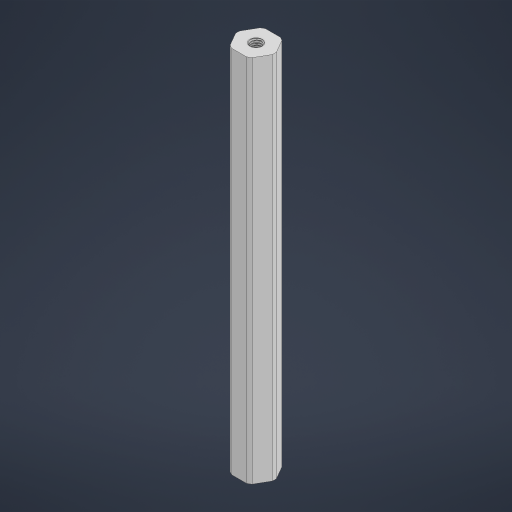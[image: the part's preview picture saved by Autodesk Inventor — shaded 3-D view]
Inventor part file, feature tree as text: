
AUTODESK INVENTOR PART (.ipt)
format: ipt  version: 2023 (Build 270158000, 158)  size: 953,344 bytes
history: native  units: in
note: dims shown in document units (in); Inventor stores cm internally (conversion verified against a paired STEP export)
features: mirror x1
ambient origin geometry x8: Origin, YZ Plane, XZ Plane, XY Plane, X Axis, Y Axis, Z Axis, Center Point
bodies: Solid1 (feature_tree)
feature tree (1):
  mirror  "Mirror2"
